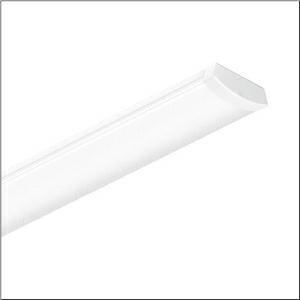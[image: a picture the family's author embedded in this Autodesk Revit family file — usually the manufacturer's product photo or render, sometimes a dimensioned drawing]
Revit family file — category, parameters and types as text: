
# Revit family: siluette_21_51ln12mkm40a3g
name_source: partatom
category: Lighting Fixtures
units: mm (PartAtom-declared; Revit-internal decimal feet)

## family parameters
Cut with Voids When Loaded = No
Host = Face
Light Source = No
Part Type = Normal
Room Calculation Point = No
Round Connector Dimension = Use Diameter
Shared = No

## types (1)
- --- (1 x LED, 2980 lm, 20.6 W, 5000K)
    Apparent Load = 21 VA
    CIE Flux Codes = 43 73 92 94 100
    Color Rendering = 80
    Color Temperature = 5000K
    Default Elevation = 1800 mm
    Description = Siluette 21, office luminaire, primary optical cover: enclosure, of PC, frosted, light emission: direct distribution, primary light characteristic: symmetric, installation type: suspended mounting, surface-mounted, LED, rated luminous flux: 5.010lm, luminous efficacy: 136lm/W, light colour: 830/840/850, colour temperature: 3000/4000/5000K, control gear: ON/OFF Multilumen, with terminal, 4-pole, mains connection: 220..240V, AC, 50/60Hz, rated input power: 37W, control gear: single battery element, housing, of sheet steel, white, length: 1.200mm, width: 152mm, height: 53mm, end cap, of PMMA, white, protection rating (complete): IP44, insulation class (complete): insulation class I (protective earthing), certification: CE, UKCA, protection symbol: D, impact resistance: IK04, permissible operating ambient temperature: +5..+40°C, standard: EN 60598-2-22, contact your sales advisor before using the luminaires in applications with unclear chemical exposure, large temperature fluctuations or condensation-forming humidity, corresponds to IFS (International Featured Standards) requirements for safety and quality in the food industry, packaging unit: 1 piece
    Height = 52 mm  [stored 0.170604 ft]
    Lamp = 1 x LED
    Lamp Light Flux = 2980 lm
    Lamp Power = 20.6 W
    Lamp count = 1
    Length = 1185 mm
    Luminous efficacy = 145 lm/W
    Manufacturer = Siteco
    ModVariant = No
    Model = 51LN12MKM40A3G
    Mounting Place = Ceiling
    Mounting Type = Pendant
    Number of Poles = 1
    OnlyDefault = Yes
    Power Factor = 1
    Product Name = Siluette 21
    Product group = office luminaire | ceiling pendant
    ProductGroupID = 903
    Protection Class = Protection class I
    Protection Degree = IP 44
    RLX_Detail_Level = 1
    RLX_Emergency_Light_Flux = 0 lm
    RLX_Emergency_Type = 0
    RLX_Emergency_Type_DB = No
    RlxData = <blob elided: 19513 chars, md5=395ee717>
    Socket = socket
    Standby Power = 0 W
    System Light Flux = 2980 lm
    System Power = 21 W
    Type Comments = individual setting: colour temperature 5000K, luminous flux: 60 % | (OFF | OFF | ON) | 200 mA
    Type Image = l_1296910.jpg
    URL = http://relux.com
    VarID = @adj_065821
    Voltage = 0 V
    Weight = 0.00 kg
    Width = 152 mm

note: [stored X ft] marks values corroborated as IEEE doubles in the binary element streams (Revit-internal decimal feet)

## geometry (parser evidence)
native form markers: Blend x4, Sweep x12
no freeform markers — native parametric forms only
